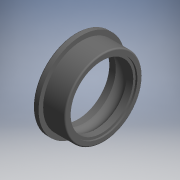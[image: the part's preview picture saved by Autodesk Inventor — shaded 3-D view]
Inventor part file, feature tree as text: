
AUTODESK INVENTOR PART (.ipt)
format: ipt  version: 2017.3 (Build 213256000, 256)  size: 146,944 bytes
history: native  units: mm (DEFAULTED — no unit token found)
features: other x14, revolve x1, sketch x1
ambient origin geometry x8: Origin, YZ Plane, XZ Plane, XY Plane, X Axis, Y Axis, Z Axis, Center Point
bodies: Solid1 (feature_tree)
feature tree (16):
  revolve  "Revolution1"  [1 undecoded]
  other  "ip_st_1_XY"
  other  "ip_st_1_YZ"
  other  "ip_st_1_ZX"
  other  "ip_st_1_X"
  other  "ip_st_1_Y"
  other  "ip_st_1_Z"
  other  "ip_st_1_Center"
  other  "ip_st_2_XY"
  other  "ip_st_2_YZ"
  other  "ip_st_2_ZX"
  other  "ip_st_2_X"
  other  "ip_st_2_Y"
  other  "ip_st_2_Z"
  other  "ip_st_2_Center"
  sketch  "Sketch_1"  dims[d0=360.0deg d1=0.0mm d2=0.0mm]
note: 1 required parameter value undecoded (feature->parameter linkage not recoverable at this tier; creation-order binding heuristic only, values carry confidence <= 0.55)
